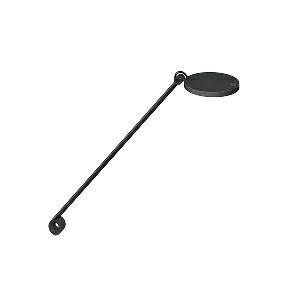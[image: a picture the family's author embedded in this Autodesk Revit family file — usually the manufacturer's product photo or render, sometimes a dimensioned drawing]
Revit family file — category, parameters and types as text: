
# Revit family: para_mi_-_mftl_102_r__940_00643978_4a3e
name_source: partatom
category: Lighting Fixtures
units: mm (PartAtom-declared; Revit-internal decimal feet)

## family parameters
Cut with Voids When Loaded = No
Host = Face
Light Source = No
Part Type = Normal
Room Calculation Point = No
Round Connector Dimension = Use Diameter
Shared = No

## types (1)
- PARA.MI - MFTL 102 R /940 (1 x LED, 600 lm, 4000K)
    Apparent Load = 7 VA
    Approval mark = CE
    CIE Flux Codes = 69 94 99 100 100
    Color Rendering = 90-100
    Color Temperature = 4000K
    Control Gear = Electronic ballast
    Default Elevation = 1800 mm
    Description = MFTL 102 R|Task luminaire|light source: LED|work equipment: Electronic plug-in transformer|connected load: 100-240 V, 50/60 Hz|Power consumption: approx. 7 W|luminous flux: 600 lm|luminous efficacy: 85 lm/W|Illuminance efficiency factor: 111 lx/W|colour temperature: Cold white, ca. 4000 K|color rendering index (CRI): >= 90|chromaticity tolerance:  3 SDCM|class of protection: II with plug-in power supply, III without plug-in power supply|technology: Continuously dimmable|luminaire body|material: Aluminium|surface: Painted|colour: Black|lamp cover: Plastic, Clear|tubular sections|material: Tubular aluminium section|surface: Painted|colour: Jet black|weight (net): approx. 0.8 kg|mains lead: 3.00 m Mains plug BS 1363, CEE 7/XVI, NEMA 1-15P|Fastening: Adaptor (accessory), Table base (accessory), Table clamp (accessory), Tap16|glare control: Reflector|special features: Automatic switchoff adjustable, Push button in luminaire head, Behaviour at net recovery adjustable|Approval mark: C - ETL - US (F. CAN U. USA), VDE - ENEC SEP LIGHT & POWER SUPPLY UNIT|
    Height = 12 mm  [stored 0.0393701 ft]
    Lamp = 1 x LED
    Lamp Light Flux = 600 lm
    Lamp count = 1
    Length = 123 mm
    Luminous efficacy = 86 lm/W
    Manufacturer = Waldmann
    ModVariant = No
    Model = 00643978
    Mounting Place = Table
    Mounting Type = Surface mounted
    Number of Poles = 1
    OnlyDefault = Yes
    Power Factor = 1
    Product Name = PARA.MI - MFTL 102 R /940
    Product group = Task luminaire (office)
    ProductGroupID = 21
    Protection Class = Protection class II
    Protection Degree = IP 40
    RLX_Detail_Level = 1
    RLX_Emergency_Light_Flux = 0 lm
    RLX_Emergency_Type = 0
    RLX_Emergency_Type_DB = No
    RlxData = <blob elided: 59009 chars, md5=35d39637>
    Socket = socket
    Standby Power = 0 W
    System Light Flux = 600 lm
    System Power = 7 W
    Type Comments = Product without accessories
    Type Image = 113150000-00643978.jpg
    URL = http://relux.com
    VarID = ---
    Voltage = 230 V
    Voltage Range = 220-240 V
    Weight = 0.00 kg
    Width = 0 mm  [stored 0 ft]

note: [stored X ft] marks values corroborated as IEEE doubles in the binary element streams (Revit-internal decimal feet)

## geometry (parser evidence)
native form markers: Blend x4, Sweep x15
no freeform markers — native parametric forms only
